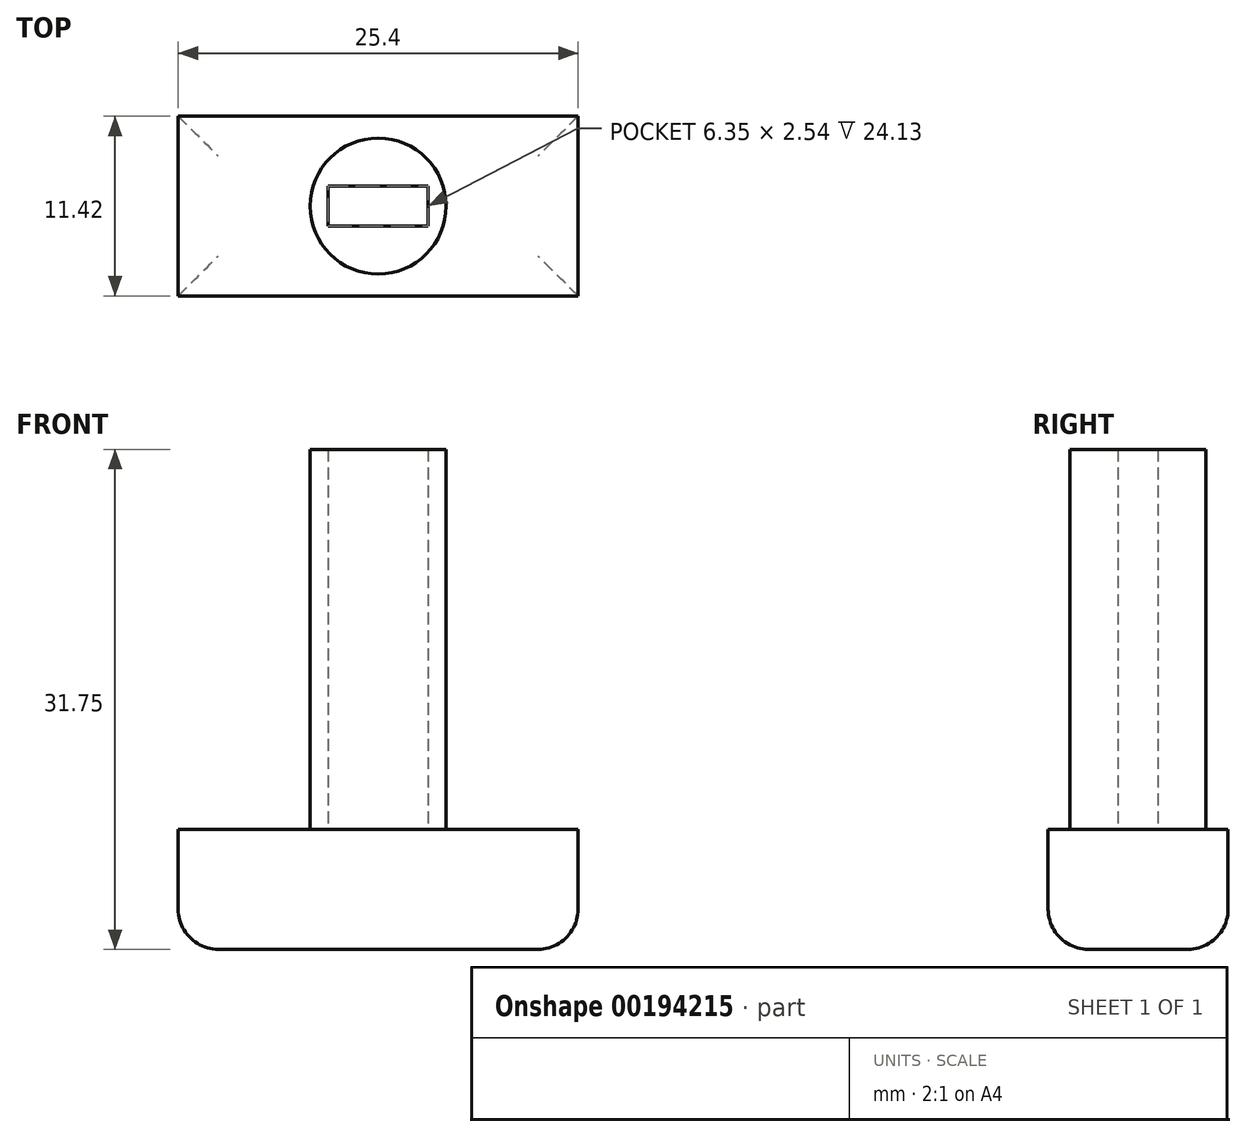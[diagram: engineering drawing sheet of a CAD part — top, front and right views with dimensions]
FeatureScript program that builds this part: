
annotation { "Feature Type Name" : "Feature", "Feature Type Description" : "" }
export const myFeature = defineFeature(function(context is Context, id is Id, definition is map)
    precondition{}
    {
        {
            var Q0;
            Q0=qCreatedBy(makeId("Top.planeOp"),FACE);
            var sketch = newSketch(context, id + "F0", { "sketchPlane" : qUnion([Q0])});
            skCircle(sketch, "E0", {"center": v(0, 0) * mm, "radius": 4.32 * mm});
            skLineSegment(sketch, "E1.bottom", {"start": v(3.18, -1.27) * mm, "end": v(-3.18, -1.27) * mm});
            skLineSegment(sketch, "E1.top", {"start": v(3.18, 1.27) * mm, "end": v(-3.18, 1.27) * mm});
            skLineSegment(sketch, "E1.left", {"start": v(3.18, -1.27) * mm, "end": v(3.18, 1.27) * mm});
            skLineSegment(sketch, "E1.right", {"start": v(-3.18, -1.27) * mm, "end": v(-3.18, 1.27) * mm});
            skSolve(sketch);
        }
        {
            var Q0;
            Q0=makeQuery(id+"F0.imprint","IMPRINT",FACE,{"disambiguationData":[TD([[makeQuery(id+"F0.imprint","IMPRINT",EDGE,{"derivedFrom":sQuery(id+"F0.wireOp",EDGE,"E0")}),1.0]])]});
            extrude(context, id + "F1", {"entities" : qUnion([Q0]), "depth" : 24.13 * mm});
        }
        {
            var Q0;
            Q0=makeQuery(id+"F1.opExtrude","CAP_FACE",FACE,{"disambiguationData":[OSD([sQuery(id+"F0.wireOp",EDGE,"E0"),sQuery(id+"F0.wireOp",EDGE,"E1.bottom"),sQuery(id+"F0.wireOp",EDGE,"E1.top"),sQuery(id+"F0.wireOp",EDGE,"E1.left"),sQuery(id+"F0.wireOp",EDGE,"E1.right")])],"isStart":true});
            var sketch = newSketch(context, id + "F2", { "sketchPlane" : qUnion([Q0])});
            skLineSegment(sketch, "E2.bottom", {"start": v(12.7, 5.72) * mm, "end": v(-12.7, 5.72) * mm});
            skLineSegment(sketch, "E2.top", {"start": v(12.7, -5.72) * mm, "end": v(-12.7, -5.72) * mm});
            skLineSegment(sketch, "E2.left", {"start": v(12.7, 5.72) * mm, "end": v(12.7, -5.72) * mm});
            skLineSegment(sketch, "E2.right", {"start": v(-12.7, 5.72) * mm, "end": v(-12.7, -5.72) * mm});
            skPoint(sketch, "E2.middle", {"position": v(0, 0) * mm});
            skSolve(sketch);
        }
        {
            var Q0;
            Q0=makeQuery(id+"F2.imprint","IMPRINT",FACE,{"disambiguationData":[TD([[makeQuery(id+"F2.imprint","IMPRINT",EDGE,{"derivedFrom":sQuery(id+"F2.wireOp",EDGE,"E2.bottom")}),1.0]])]});
            var Q1;
            Q1=makeQuery(id+"F2.imprint","IMPRINT",FACE,{"disambiguationData":[TD([[makeQuery(id+"F2.imprint","IMPRINT",EDGE,{"derivedFrom":makeQuery(id+"F1.opExtrude","CAP_EDGE",EDGE,{"disambiguationData":[OSD([sQuery(id+"F0.wireOp",EDGE,"E0")])],"isStart":true})}),-1.0]])]});
            var Q2;
            Q2=makeQuery(id+"F2.imprint","IMPRINT",FACE,{"disambiguationData":[TD([[makeQuery(id+"F2.imprint","IMPRINT",EDGE,{"derivedFrom":makeQuery(id+"F1.opExtrude","CAP_EDGE",EDGE,{"disambiguationData":[OSD([sQuery(id+"F0.wireOp",EDGE,"E1.bottom")])],"isStart":true})}),1.0]])]});
            extrude(context, id + "F3", {"entities" : qUnion([Q0, Q1, Q2]), "operationType" : NewBodyOperationType.ADD, "depth" : 7.62 * mm});
        }
        {
            var Q0;
            Q0=makeQuery(id+"F3.opExtrude","CAP_FACE",FACE,{"disambiguationData":[OSD([sQuery(id+"F2.wireOp",EDGE,"E2.bottom"),sQuery(id+"F2.wireOp",EDGE,"E2.top"),sQuery(id+"F2.wireOp",EDGE,"E2.left"),sQuery(id+"F2.wireOp",EDGE,"E2.right")])],"isStart":false});
            fillet(context, id + "F4", {"entities" : qUnion([Q0]), "radius" : 2.54 * mm, "tangentPropagation" : true, "allowEdgeOverflow" : false});
        }
    });
